# Revit family: RN 13110 Sicherheitsgarnitur
name_source: partatom
category: Rohrzubehör
units: mm (PartAtom-declared; Revit-internal decimal feet)

## family parameters
Arbeitsebenenbasiert = Nein
Beim Laden mit Abzugskörper schneiden = Nein
Bemaßung runder Anschluss = Durchmesser verwenden
Gemeinsam genutzt = Nein
Immer vertikal = Ja
Teiletyp = Ventil - Zerlegung in

## types (3) — shared parameters
1.010.00.2 Blattnummer der Richtlinie = 17
1.010.00.3 Ausgabedatum (Monat) der Richtlinie = 201601
1.010.00.4 Herstellername = R. Nussbaum AG
1.010.00.5 Revisionsdatum der Datei = 20190528
1.010.00.6 Webadresse des Herstellers = http://www.nussbaum.ch
1.100.00.3 Sortiernummer für Anzeigereihenfolge = 5
1.100.00.4 Produktbezeichnung = Sicherheitsarmaturen
1.960/3L.00.8 Link (URL) = https://www.nussbaum.ch
17.700.00.4 Armaturentyp = 6
17.700.00.7 Maximale Betriebstemperatur TB [°C] = 90
17.700.00.8 Maximaler Betriebsdruck (Arbeitsdruck) ps [1.0 · 105 Pa] = 10
CONNECTOR2_DIAMETER_dZ_0r = 20 mm
Connector Visibility = Nein
EnclosingSpace Visibility = Nein
Hersteller = R. Nussbauzm AG
URL = https://www.nussbaum.ch

## per-type parameters (varying)
- DN 20: 1.800.00.3 TGA-Nummer=0050140000000000000000000000020070000000000000000100000000; 1.810.00.3 Hersteller-Bestellnummer=13110.05; 1.810.00.4 DATANORM-Nummer=13110.05; 1.810.00.5 StLB-Nummer=612.164; 1.810.00.6 GTIN-Nummer=7612945737212; 17.700.00.30 Produktbeschreibung=13110.05, Sicherheitsgarnitur, Sicherheitsventil 6 bar fest eingestellt, DN=20, R; 17.700.00.5 Nennweite DN=20; 17.700.00.6 kvs-Wert [m3/h]=11.4; CONNECTOR0_DIAMETER_dZ_0r=20 mm; CONNECTOR0_dZ_00=39 mm; CONNECTOR0_dZ_01=24 mm; CONNECTOR0_ref_dZ=24 mm; CONNECTOR1_DIAMETER_dZ_0r=20 mm; CONNECTOR1_dZ_00=31 mm; CONNECTOR1_dZ_01=46 mm; CONNECTOR1_ref_dZ=31 mm; CONNECTOR2_dZ_00=14 mm  [stored 0.0459318 ft]; CONNECTOR2_dZ_01=1 mm  [stored 0.00328084 ft]; CONNECTOR2_ref_dX=70 mm; CONNECTOR2_ref_dZ=1 mm  [stored 0.00328084 ft]; Modell=13110.05; R. Nussbaum AG 13110.05 de Visibility=Ja; R. Nussbaum AG 13110.06 de Visibility=Nein; R. Nussbaum AG 13110.07 de Visibility=Nein; Typenkommentare=SicherheitsgarniturDN 20
- DN 25: 1.800.00.3 TGA-Nummer=0050140000000000000000000000020070000000000000000200000000; 1.810.00.3 Hersteller-Bestellnummer=13110.06; 1.810.00.4 DATANORM-Nummer=13110.06; 1.810.00.5 StLB-Nummer=612.165; 1.810.00.6 GTIN-Nummer=7612945737526; 17.700.00.30 Produktbeschreibung=13110.06, Sicherheitsgarnitur, Sicherheitsventil 6 bar fest eingestellt, DN=25, R; 17.700.00.5 Nennweite DN=25; 17.700.00.6 kvs-Wert [m3/h]=17.4; CONNECTOR0_DIAMETER_dZ_0r=25 mm  [stored 0.082021 ft]; CONNECTOR0_dZ_00=47 mm; CONNECTOR0_dZ_01=30 mm; CONNECTOR0_ref_dZ=30 mm; CONNECTOR1_DIAMETER_dZ_0r=25 mm  [stored 0.082021 ft]; CONNECTOR1_dZ_00=36 mm; CONNECTOR1_dZ_01=53 mm; CONNECTOR1_ref_dZ=36 mm; CONNECTOR2_dZ_00=13 mm; CONNECTOR2_dZ_01=2 mm  [stored 0.00656168 ft]; CONNECTOR2_ref_dX=75 mm; CONNECTOR2_ref_dZ=2 mm  [stored 0.00656168 ft]; Modell=13110.06; R. Nussbaum AG 13110.05 de Visibility=Nein; R. Nussbaum AG 13110.06 de Visibility=Ja; R. Nussbaum AG 13110.07 de Visibility=Nein; Typenkommentare=SicherheitsgarniturDN 25
- DN 32: 1.800.00.3 TGA-Nummer=0050140000000000000000000000020070000000000000000300000000; 1.810.00.3 Hersteller-Bestellnummer=13110.07; 1.810.00.4 DATANORM-Nummer=13110.07; 1.810.00.5 StLB-Nummer=612.166; 1.810.00.6 GTIN-Nummer=7612945735102; 17.700.00.30 Produktbeschreibung=13110.07, Sicherheitsgarnitur, Sicherheitsventil 6 bar fest eingestellt, DN=32, R; 17.700.00.5 Nennweite DN=32; 17.700.00.6 kvs-Wert [m3/h]=30; CONNECTOR0_DIAMETER_dZ_0r=32 mm; CONNECTOR0_dZ_00=55 mm; CONNECTOR0_dZ_01=36 mm; CONNECTOR0_ref_dZ=36 mm; CONNECTOR1_DIAMETER_dZ_0r=32 mm; CONNECTOR1_dZ_00=41 mm; CONNECTOR1_dZ_01=60 mm; CONNECTOR1_ref_dZ=41 mm; CONNECTOR2_dZ_00=11 mm; CONNECTOR2_dZ_01=4 mm  [stored 0.0131234 ft]; CONNECTOR2_ref_dX=80 mm; CONNECTOR2_ref_dZ=4 mm  [stored 0.0131234 ft]; Modell=13110.07; R. Nussbaum AG 13110.05 de Visibility=Nein; R. Nussbaum AG 13110.06 de Visibility=Nein; R. Nussbaum AG 13110.07 de Visibility=Ja; Typenkommentare=SicherheitsgarniturDN 32

note: [stored X ft] marks values corroborated as IEEE doubles in the binary element streams (Revit-internal decimal feet)

## geometry (parser evidence)
native form markers: Sweep x1
no freeform markers — native parametric forms only
